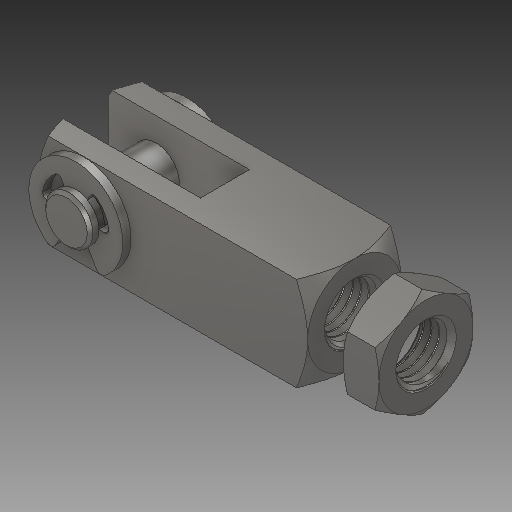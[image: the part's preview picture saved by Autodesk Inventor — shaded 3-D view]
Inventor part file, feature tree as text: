
AUTODESK INVENTOR PART (.ipt)
format: ipt  version: 2018 (Build 220112000, 112)  size: 1,035,264 bytes
history: native  units: in
note: dims shown in document units (in); Inventor stores cm internally (conversion verified against a paired STEP export)
features: other x3, revolve x1, mirror x1
ambient origin geometry x8: Origin, YZ Plane, XZ Plane, XY Plane, X Axis, Y Axis, Z Axis, Center Point
bodies: Solid1 (feature_tree), Solid2 (feature_tree), Solid3 (feature_tree), Solid4 (feature_tree), Solid5 (feature_tree)
feature tree (5):
  other  "Cut-Extrude5"
  revolve  "Revolve1"  [1 undecoded]
  other  "Boss-Extrude2"
  mirror  "Mirror1"
  other  "Cut-Extrude9"
note: 1 required parameter value undecoded (feature->parameter linkage not recoverable at this tier; creation-order binding heuristic only, values carry confidence <= 0.55)
